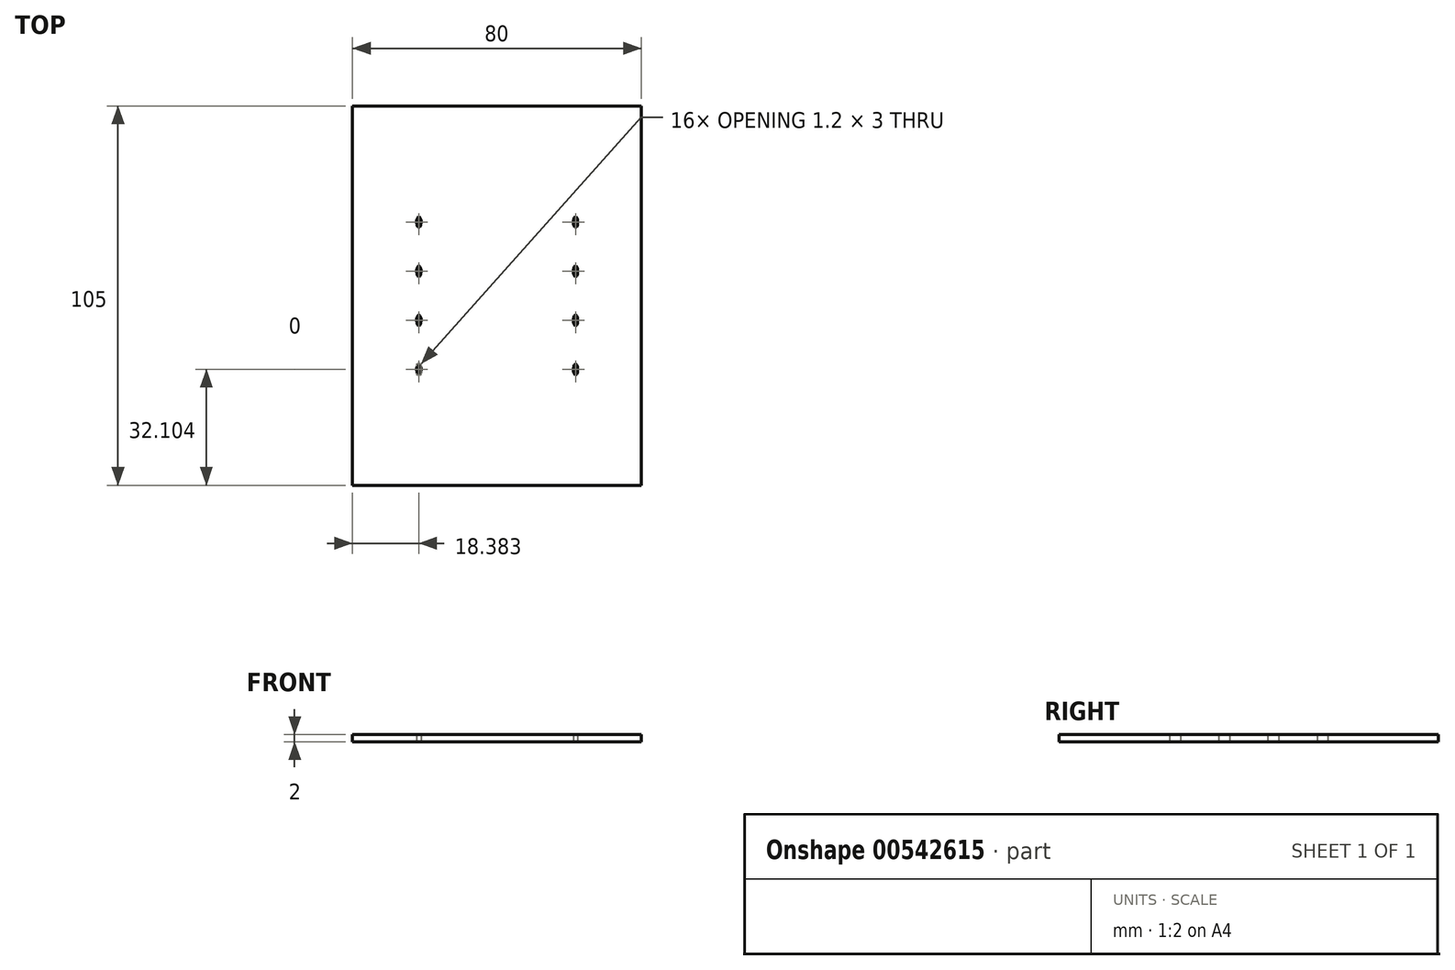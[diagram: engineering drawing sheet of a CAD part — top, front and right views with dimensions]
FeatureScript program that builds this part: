
annotation { "Feature Type Name" : "Feature", "Feature Type Description" : "" }
export const myFeature = defineFeature(function(context is Context, id is Id, definition is map)
    precondition{}
    {
        {
            var Q0;
            Q0=qCreatedBy(makeId("Top.planeOp"),FACE);
            var sketch = newSketch(context, id + "F0", { "sketchPlane" : qUnion([Q0])});
            skLineSegment(sketch, "E0", {"start": v(-33.4, 45.73) * mm, "end": v(-33.4, -59.27) * mm});
            skLineSegment(sketch, "E1", {"start": v(-33.4, -59.27) * mm, "end": v(46.6, -59.27) * mm});
            skLineSegment(sketch, "E2", {"start": v(46.6, -59.27) * mm, "end": v(46.6, 45.73) * mm});
            skLineSegment(sketch, "E3", {"start": v(46.6, 45.73) * mm, "end": v(-33.4, 45.73) * mm});
            skPoint(sketch, "E4", {"position": v(28.38, 13.63) * mm});
            skPoint(sketch, "E5", {"position": v(28.38, 0.03) * mm});
            skPoint(sketch, "E6", {"position": v(28.38, -13.57) * mm});
            skPoint(sketch, "E7", {"position": v(28.38, -27.17) * mm});
            skPoint(sketch, "E8", {"position": v(-15.02, 13.63) * mm});
            skPoint(sketch, "E9", {"position": v(-15.02, 0) * mm});
            skPoint(sketch, "E10", {"position": v(-15.02, -13.57) * mm});
            skPoint(sketch, "E11", {"position": v(-15.02, -27.17) * mm});
            skEllipse(sketch, "E12", {"center": v(-15.02, 13.63) * mm, "majorRadius": 1.5 * mm, "minorRadius": 0.6 * mm, "majorAxis": v(0, 1)});
            skEllipse(sketch, "E13", {"center": v(-15.02, 0) * mm, "majorRadius": 1.5 * mm, "minorRadius": 0.6 * mm, "majorAxis": v(0, 1)});
            skEllipse(sketch, "E14", {"center": v(-15.02, -13.57) * mm, "majorRadius": 1.5 * mm, "minorRadius": 0.6 * mm, "majorAxis": v(0, 1)});
            skEllipse(sketch, "E15", {"center": v(-15.02, -27.17) * mm, "majorRadius": 1.5 * mm, "minorRadius": 0.6 * mm, "majorAxis": v(0, 1)});
            skEllipse(sketch, "E16", {"center": v(28.38, -27.17) * mm, "majorRadius": 1.5 * mm, "minorRadius": 0.6 * mm, "majorAxis": v(0, 1)});
            skEllipse(sketch, "E17", {"center": v(28.38, -13.57) * mm, "majorRadius": 0.6 * mm, "minorRadius": 1.5 * mm, "majorAxis": v(1, 0)});
            skEllipse(sketch, "E18", {"center": v(28.38, 13.63) * mm, "majorRadius": 0.6 * mm, "minorRadius": 1.5 * mm, "majorAxis": v(1, 0)});
            skEllipse(sketch, "E19", {"center": v(28.38, 0.03) * mm, "majorRadius": 0.6 * mm, "minorRadius": 1.5 * mm, "majorAxis": v(1, 0)});
            skSolve(sketch);
        }
        {
            var Q0;
            Q0 = qSketchRegion(id + "F0", true);
            extrude(context, id + "F1", {"entities" : qUnion([Q0]), "depth" : 2 * mm, "offsetDistance" : 25 * mm});
        }
    });
